# Revit family: Combination_Paper_Towel_Dryer_Waste-Bobrick-TrimLineSeries_B-38030_Series
name_source: partatom
category: Specialty Equipment
units: mm (PartAtom-declared; Revit-internal decimal feet)

## family parameters
Cut with Voids When Loaded = No
Host = Face
OmniClass Number = 23.40.20.21.17
OmniClass Title = Paper Towel Dispensers, Disposal Units
Part Type = Normal
Room Calculation Point = No
Round Connector Dimension = Use Diameter
Shared = Yes

## types (2) — shared parameters
ADA Compliant = Yes
Assembly Code = C1030200
Default Elevation = 44"
Description = TrimLineSeries™ Recessed Paper Towel Dispenser, Automatic Hand Dryer, and Waste Bin (3-IN-1 UNIT)
Frequency = 60 Hz
Height = 57"
Installation Type = Recessed
Length = 4 1/2"
Manufacturer = Bobrick Washroom Equipment, Inc.
Material = Stainless Steel-Bobrick-Type 304-Satin
Phase = 1
Price = Prices may vary. Please consult Manufacturer Representative for most up-to-date price list.
Product Documentation Link = https://www.bobrick.com
Product Page URL = https://washroominc.com
Specification = Recessed Paper Towel Dispenser, Automatic Hand Dryer, And Waste Bin (3-in-1 unit) shall be type-304 stainless steel with all-welded construction; exposed surfaces shall have satin finish. Doors shall be 1.2mm (18-gauge); have 14mm (9/16") 90° return edges; be secured to cabinet with concealed, full-length stainless steel piano-hinges; and equipped with a stainless steel cable door-swing limiter and two flush tumbler locks per door keyed like other Bobrick washroom accessories. Paper towel dispenser shall be capable of dispensing 600 multifold or 450 C-fold paper towels. Unit equipped with TowelMate consisting of a 90° return towel guide angle inside cabinet to prevent paper towels from falling forward out when door is opened for servicing and a Nylon Rod across the center of the towel tray to dispense paper towels one at a time. Waste bin shall be furnished with a removable, leak-proof, rigid molded plastic waste-container with a capacity of 13.7 liters (3.6 gal.). Directed air nozzles shall prevent dryer from blowing into waste bin. Hand dryer shall have a one-piece,18-8, type-304, 0.8mm (22-gauge) stainless steel cover. Dryer mounting base shall be 1.5mm (20-gauge) plated steel with three 6mm (0.236") diameter mounting holes. Fan housings shall be fire-retardant molded black plastic. Dryer shall be equipped with dual air outlets that run through two vertical ducts and out the black plastic nozzles under the towel dispenser. Motor shall be 1/7 hp, universal type on resilient mounting with sealed ball bearing at drive-shaft end and self-lubricating sleeve bearing at nondrive end; equipped with automatic thermal-overload switch. Heating elements shall be located on outlet side of fan, shall heat air without hot spots, be inaccessible to vandals, and protected by an automatic thermal-overload switch. The dryer will be controlled by the activation sensor which is part of the electronic control. The electronic control will never allow the dryer motor to be hotter than 70°C. There are two modes of operation, dryer promotion and paper promotion. Dryer promotion mode, the dryer shall turn on when hands are held under air-outlet opening and across path of sensor. Paper promotion mode, there will be a three (3) second delay between seeing the hands and when the dryer turns on. Dryer shall turn off automatically when hands are removed. Sensor shall automatically shut dryer off approximately 1-1/2 minutes after dryer turns on if an inanimate object is placed in activation zone. After inanimate object is removed, electronic sensor shall automatically reset itself and dryer shall operate normally. The electronic control will have an LED that will flash green when the dryer is ready, be solid green when the dryer is running and be solid red when the dryer is not ready. Unit shall VDE approved, CE marked and cUListed. Unit shall comply with EU Directive "Restriction of Hazardous Substance" (ROHS) requirements for non-use of certain hazardous substances in the production of electronic products. Unit shall be protected by a limited 1-year warranty from date of purchase on all parts except motor brushes. Recessed Paper Towel Dispenser, Automatic Hand Dryer, and Waste Bin (3-in-1 unit) shall be Model B-38030 of Bobrick Washroom Equipment, Inc., Clifton Park, New York; Jackson, Tennessee; Los Angeles, California; Bobrick Washroom
Equipment Company, Scarborough, Ontario; Bobrick Washroom Equipment Pty. Ltd., Australia; and Bobrick Washroom Equipment Limited, United Kingdom.
URL = http://www.bobrick.com
Warranty Information = 1-Year Limited Warranty
Width = 15 5/8"

## per-type parameters (varying)
| type | Amperage | Connector Description | Voltage | Wattage |
| B-38030 230V | 4 A | 240V Electrical Connection | 230 V | 875 W |
| B-38030 115V | 8 A | 208V Electrical Connection | 115 V | 920 W |

note: column(s) folded — value = type name in every type: Model

## geometry (parser evidence)
native form markers: Blend x2, Sweep x3
no freeform markers — native parametric forms only
